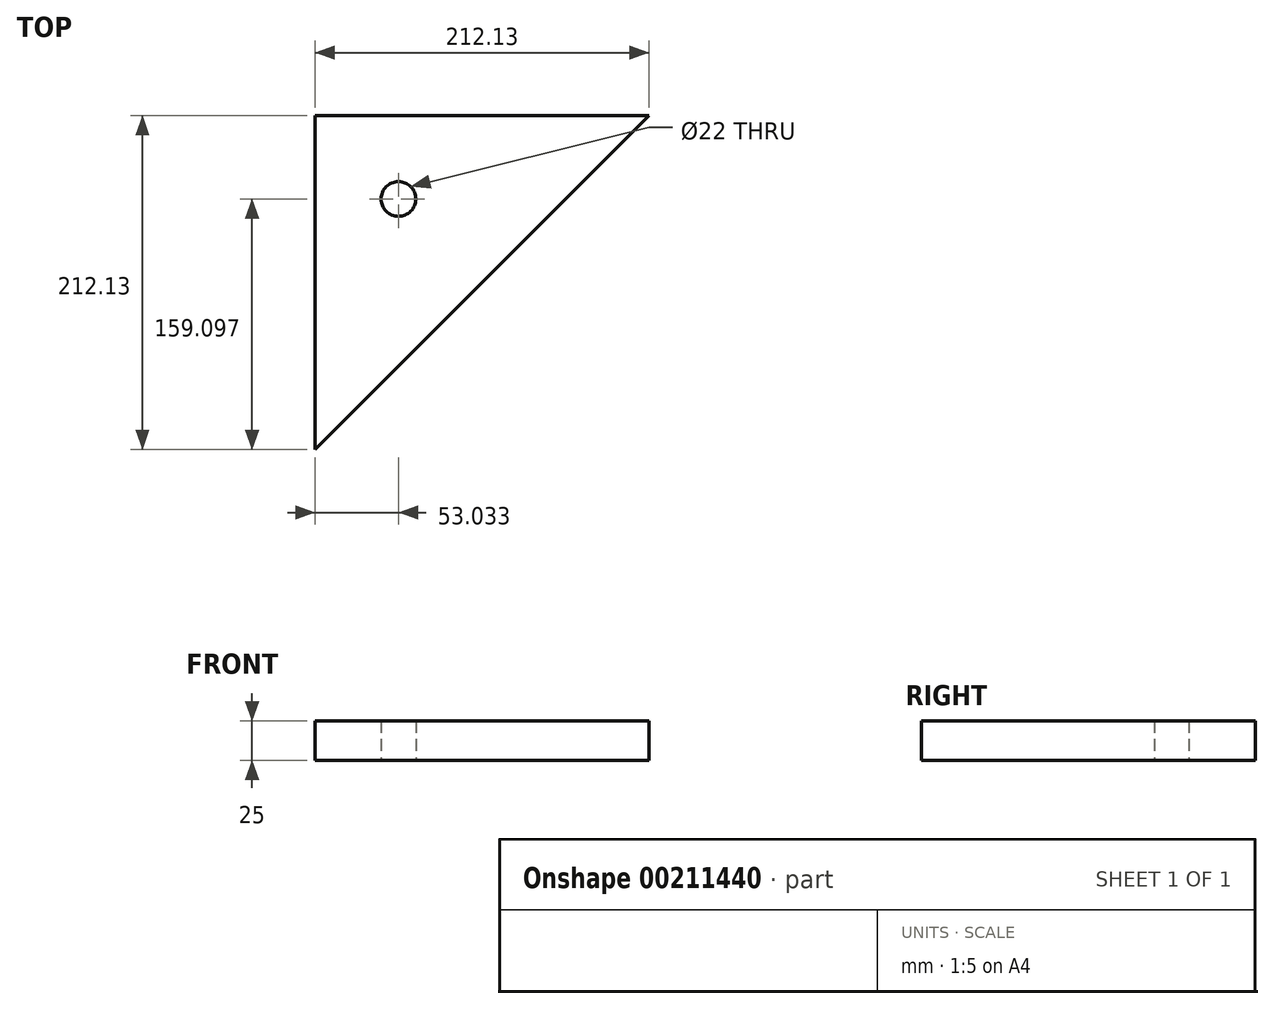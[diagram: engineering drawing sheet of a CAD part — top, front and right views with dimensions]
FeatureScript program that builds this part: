
annotation { "Feature Type Name" : "Feature", "Feature Type Description" : "" }
export const myFeature = defineFeature(function(context is Context, id is Id, definition is map)
    precondition{}
    {
        {
            var Q0;
            Q0=qCreatedBy(makeId("Top.planeOp"),FACE);
            var sketch = newSketch(context, id + "F0", { "sketchPlane" : qUnion([Q0])});
            skLineSegment(sketch, "E0", {"start": v(0, 0) * mm, "end": v(0, -212.13) * mm});
            skLineSegment(sketch, "E1", {"start": v(0, -212.13) * mm, "end": v(212.13, 0) * mm});
            skLineSegment(sketch, "E2", {"start": v(212.13, 0) * mm, "end": v(0, 0) * mm});
            skLineSegment(sketch, "E3", {"start": v(106.07, -106.07) * mm, "end": v(0, 0) * mm, "construction": true});
            skCircle(sketch, "E4", {"center": v(53.03, -53.03) * mm, "radius": 11 * mm});
            skSolve(sketch);
        }
        {
            var Q0;
            Q0 = qSketchRegion(id + "F0", true);
            extrude(context, id + "F1", {"entities" : qUnion([Q0]), "depth" : 25 * mm});
        }
    });
